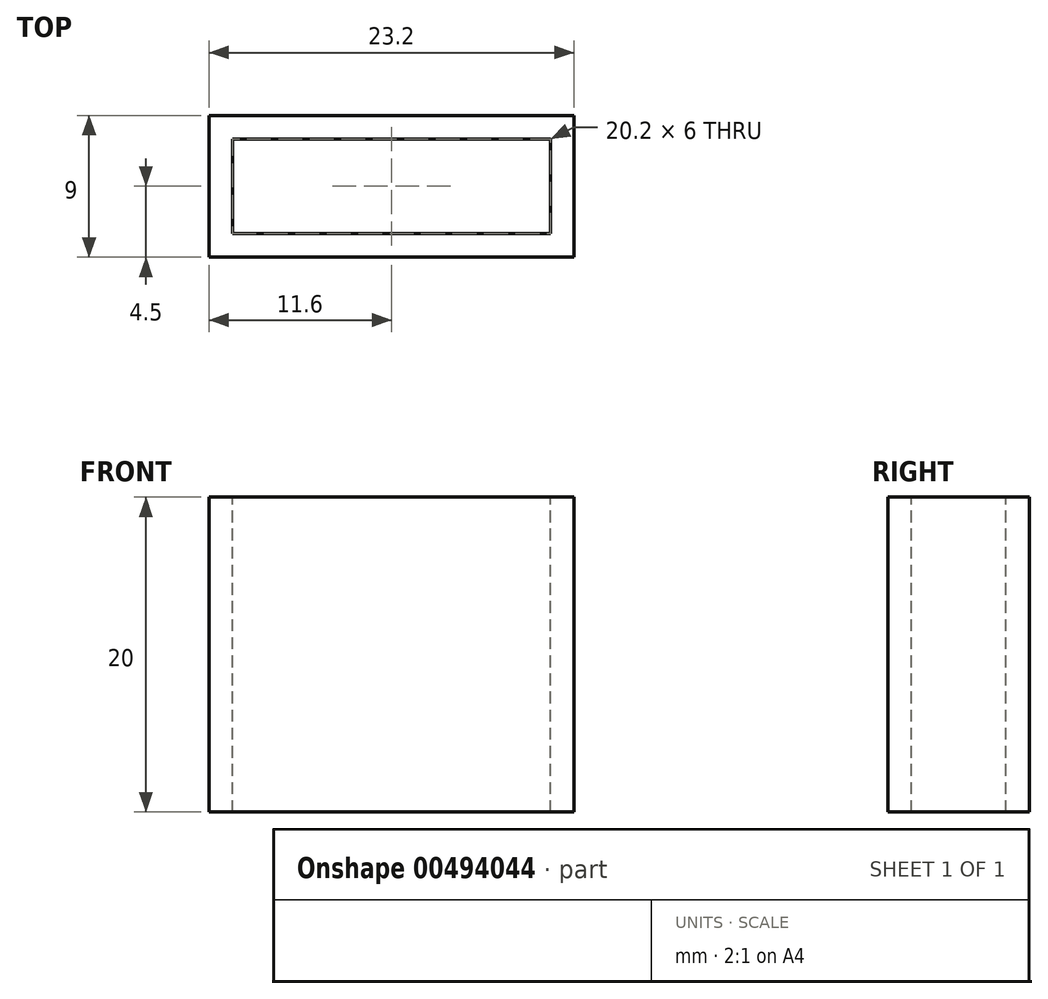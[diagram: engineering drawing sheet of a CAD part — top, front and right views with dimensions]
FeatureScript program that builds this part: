
annotation { "Feature Type Name" : "Feature", "Feature Type Description" : "" }
export const myFeature = defineFeature(function(context is Context, id is Id, definition is map)
    precondition{}
    {
        {
            var Q0;
            Q0=qCreatedBy(makeId("Front.planeOp"),FACE);
            var sketch = newSketch(context, id + "F0", { "sketchPlane" : qUnion([Q0])});
            skLineSegment(sketch, "E0.bottom", {"start": v(11.6, -10) * mm, "end": v(-11.6, -10) * mm});
            skLineSegment(sketch, "E0.top", {"start": v(11.6, 10) * mm, "end": v(-11.6, 10) * mm});
            skLineSegment(sketch, "E0.left", {"start": v(11.6, -10) * mm, "end": v(11.6, 10) * mm});
            skLineSegment(sketch, "E0.right", {"start": v(-11.6, -10) * mm, "end": v(-11.6, 10) * mm});
            skPoint(sketch, "E0.middle", {"position": v(0, 0) * mm});
            skSolve(sketch);
        }
        {
            var Q0;
            Q0=makeQuery(id+"F0.imprint","IMPRINT",FACE,{"disambiguationData":[TD([[makeQuery(id+"F0.imprint","IMPRINT",EDGE,{"derivedFrom":sQuery(id+"F0.wireOp",EDGE,"E0.bottom")}),-1.0]])]});
            extrude(context, id + "F1", {"entities" : qUnion([Q0]), "depth" : 9 * mm});
        }
        {
            var Q0;
            Q0=makeQuery(id+"F1.opExtrude","SWEPT_FACE",FACE,{"disambiguationData":[OSD([sQuery(id+"F0.wireOp",EDGE,"E0.top")])]});
            var Q1;
            Q1=makeQuery(id+"F1.opExtrude","SWEPT_FACE",FACE,{"disambiguationData":[OSD([sQuery(id+"F0.wireOp",EDGE,"E0.bottom")])]});
            shell(context, id + "F2", {"entities" : qUnion([Q0, Q1]), "thickness" : 1.5 * mm});
        }
    });
